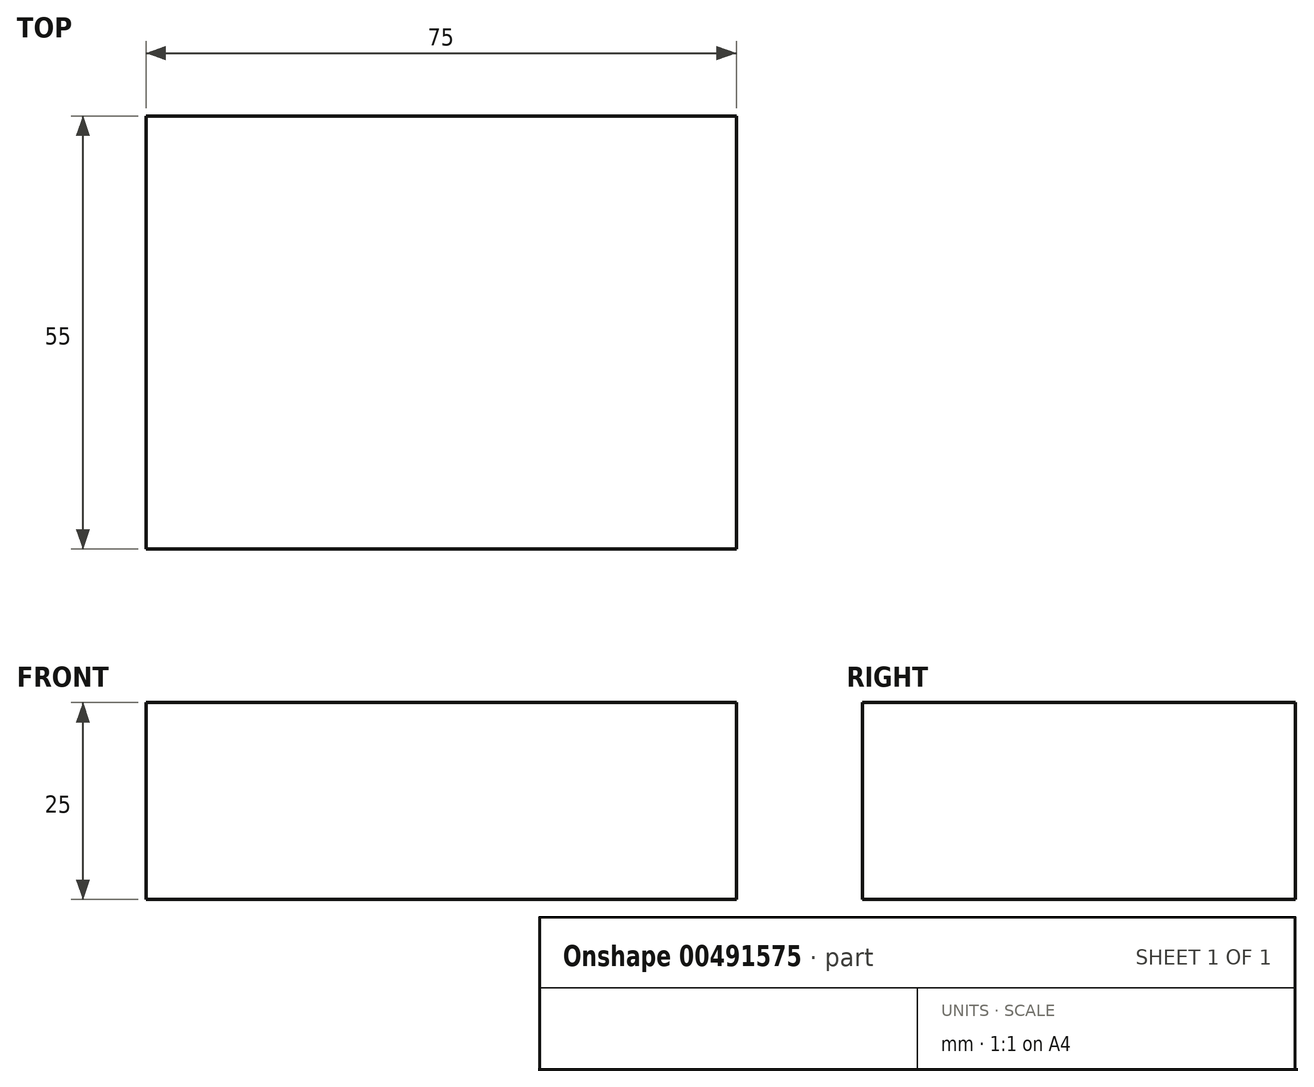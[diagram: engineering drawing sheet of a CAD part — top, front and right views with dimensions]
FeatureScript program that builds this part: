
annotation { "Feature Type Name" : "Feature", "Feature Type Description" : "" }
export const myFeature = defineFeature(function(context is Context, id is Id, definition is map)
    precondition{}
    {
        {
            var Q0;
            Q0=qCreatedBy(makeId("Top.planeOp"),FACE);
            var sketch = newSketch(context, id + "F0", { "sketchPlane" : qUnion([Q0])});
            skLineSegment(sketch, "E0.bottom", {"start": v(43.5, 33.25) * mm, "end": v(-43.5, 33.25) * mm, "construction": true});
            skLineSegment(sketch, "E0.top", {"start": v(43.5, -33.25) * mm, "end": v(-43.5, -33.25) * mm, "construction": true});
            skLineSegment(sketch, "E0.left", {"start": v(43.5, 33.25) * mm, "end": v(43.5, -33.25) * mm, "construction": true});
            skLineSegment(sketch, "E0.right", {"start": v(-43.5, 33.25) * mm, "end": v(-43.5, -33.25) * mm, "construction": true});
            skPoint(sketch, "E0.middle", {"position": v(0, 0) * mm});
            skLineSegment(sketch, "E1", {"start": v(-43.5, 0) * mm, "end": v(43.5, 0) * mm, "construction": true});
            skLineSegment(sketch, "E2", {"start": v(0, 33.25) * mm, "end": v(0, -33.25) * mm, "construction": true});
            skLineSegment(sketch, "E3.bottom", {"start": v(-37.5, 27.5) * mm, "end": v(37.5, 27.5) * mm});
            skLineSegment(sketch, "E3.top", {"start": v(-37.5, -27.5) * mm, "end": v(37.5, -27.5) * mm});
            skLineSegment(sketch, "E3.left", {"start": v(-37.5, 27.5) * mm, "end": v(-37.5, -27.5) * mm});
            skLineSegment(sketch, "E3.right", {"start": v(37.5, 27.5) * mm, "end": v(37.5, -27.5) * mm});
            skSolve(sketch);
        }
        {
            var Q0;
            Q0=makeQuery(id+"F0.imprint","IMPRINT",FACE,{"disambiguationData":[TD([[makeQuery(id+"F0.imprint","IMPRINT",EDGE,{"derivedFrom":sQuery(id+"F0.wireOp",EDGE,"E3.bottom")}),-1.0]])]});
            extrude(context, id + "F1", {"entities" : qUnion([Q0]), "depth" : 25 * mm, "offsetDistance" : 25 * mm});
        }
    });
